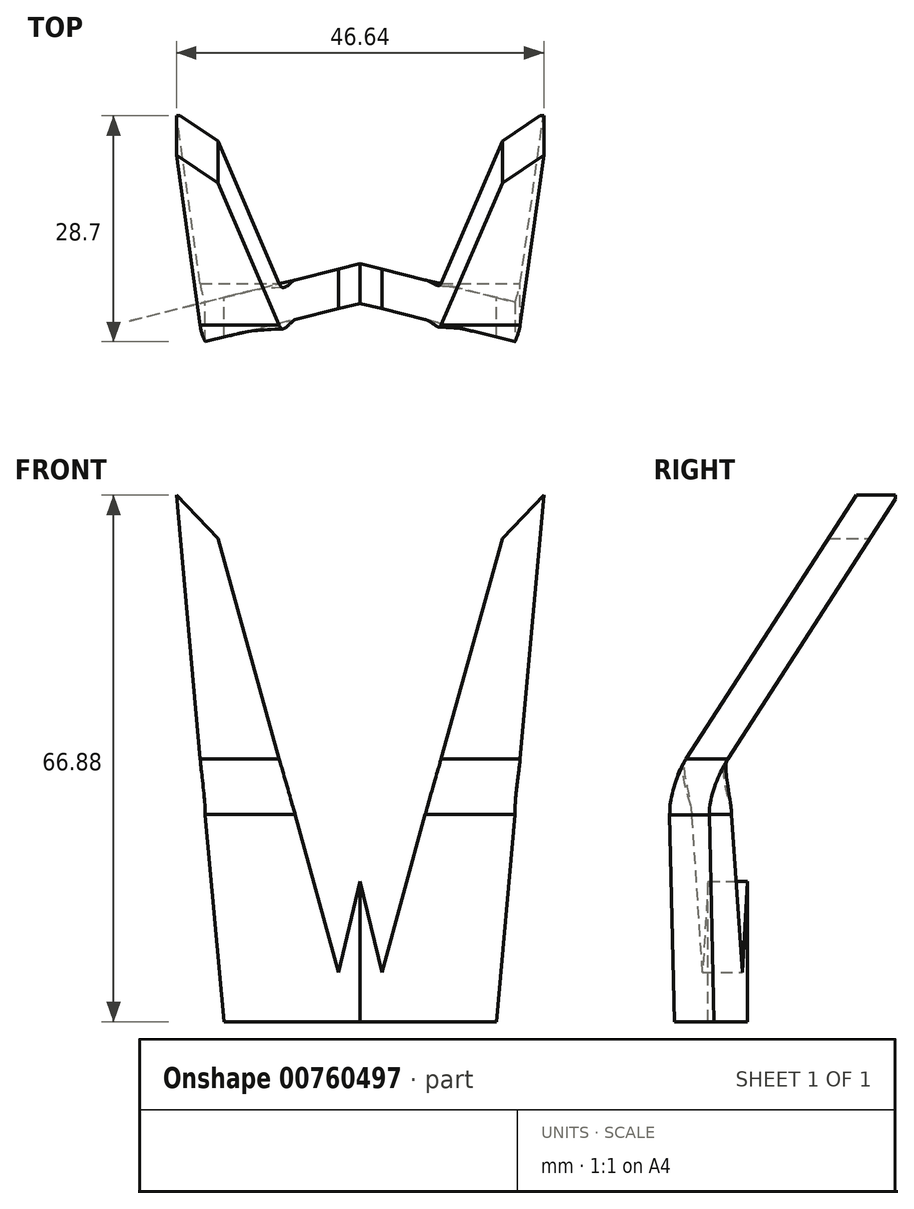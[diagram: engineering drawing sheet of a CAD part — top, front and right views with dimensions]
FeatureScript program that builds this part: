
annotation { "Feature Type Name" : "Feature", "Feature Type Description" : "" }
export const myFeature = defineFeature(function(context is Context, id is Id, definition is map)
    precondition{}
    {
        {
            var Q0;
            Q0=qCreatedBy(makeId("Front.planeOp"),FACE);
            var sketch = newSketch(context, id + "F0", { "sketchPlane" : qUnion([Q0])});
            skPoint(sketch, "E0.end.orphan", {"position": v(-20.31, 0) * mm});
            skLineSegment(sketch, "E1", {"start": v(-19.7, -7.18) * mm, "end": v(-18.06, -25.46) * mm});
            skLineSegment(sketch, "E2", {"start": v(-18.06, 27.96) * mm, "end": v(-23.32, 33.48) * mm});
            skLineSegment(sketch, "E3", {"start": v(-18.06, -25.46) * mm, "end": v(0, -33.48) * mm});
            skLineSegment(sketch, "E4.MirrorCS", {"start": v(18.06, 27.96) * mm, "end": v(23.32, 33.48) * mm});
            skLineSegment(sketch, "E5.MirrorCS", {"start": v(23.32, 33.48) * mm, "end": v(20.33, 0) * mm});
            skLineSegment(sketch, "E6.MirrorCS", {"start": v(18.06, -25.46) * mm, "end": v(0, -33.48) * mm});
            skPoint(sketch, "E7.MirrorCS.end.orphan", {"position": v(6.52, -25.46) * mm});
            skPoint(sketch, "E7.MirrorCS.start.orphan", {"position": v(18.06, 27.96) * mm});
            skLineSegment(sketch, "E8", {"start": v(-18.06, 27.96) * mm, "end": v(-10.27, 0) * mm});
            skPoint(sketch, "E8.endSnap0", {"position": v(-3.26, -18.56) * mm});
            skPoint(sketch, "E9.orphan", {"position": v(-6.52, -25.46) * mm});
            skPoint(sketch, "E10.orphan", {"position": v(0, -11.66) * mm});
            skLineSegment(sketch, "E11", {"start": v(0, -11.66) * mm, "end": v(-3.26, -25.2) * mm});
            skLineSegment(sketch, "E12.MirrorCS", {"start": v(18.06, 27.96) * mm, "end": v(10.27, 0) * mm});
            skLineSegment(sketch, "E13.MirrorCS", {"start": v(0, -11.66) * mm, "end": v(3.26, -25.2) * mm});
            skLineSegment(sketch, "E14", {"start": v(-20.31, 0) * mm, "end": v(-10.27, 0) * mm});
            skLineSegment(sketch, "E15.trimOffspring", {"start": v(10.27, 0) * mm, "end": v(20.33, 0) * mm});
            skLineSegment(sketch, "E16", {"start": v(-19.7, -7.18) * mm, "end": v(-8.28, -7.18) * mm});
            skLineSegment(sketch, "E17.trimOffspring", {"start": v(8.28, -7.18) * mm, "end": v(19.7, -7.18) * mm});
            skLineSegment(sketch, "E18.trimOffspring", {"start": v(8.28, -7.18) * mm, "end": v(3.26, -25.2) * mm});
            skLineSegment(sketch, "E19.trimOffspring", {"start": v(19.7, -7.18) * mm, "end": v(18.06, -25.46) * mm});
            skLineSegment(sketch, "E20.trimOffspring", {"start": v(-8.28, -7.18) * mm, "end": v(-3.26, -25.2) * mm});
            skLineSegment(sketch, "E21", {"start": v(-23.32, 33.48) * mm, "end": v(-20.31, 0) * mm});
            skLineSegment(sketch, "E22", {"start": v(0, -33.48) * mm, "end": v(0, -11.66) * mm});
            skPoint(sketch, "E23", {"position": v(-18.06, -25.46) * mm});
            skPoint(sketch, "E24", {"position": v(18.06, -25.46) * mm});
            skPoint(sketch, "E25", {"position": v(0, -33.48) * mm});
            skSolve(sketch);
        }
        {
            var Q0;
            Q0=makeQuery(id+"F0.imprint","IMPRINT",FACE,{"disambiguationData":[TD([[makeQuery(id+"F0.imprint","IMPRINT",EDGE,{"derivedFrom":sQuery(id+"F0.wireOp",EDGE,"E2")}),1.0]])]});
            var Q1;
            Q1=makeQuery(id+"F0.imprint","IMPRINT",FACE,{"disambiguationData":[TD([[makeQuery(id+"F0.imprint","IMPRINT",EDGE,{"derivedFrom":sQuery(id+"F0.wireOp",EDGE,"E4.MirrorCS")}),-1.0]])]});
            var Q2;
            Q2=makeQuery(id+"F0.imprint","IMPRINT",FACE,{"disambiguationData":[TD([[makeQuery(id+"F0.imprint","IMPRINT",EDGE,{"derivedFrom":sQuery(id+"F0.wireOp",EDGE,"E6.MirrorCS")}),-1.0]])]});
            extrude(context, id + "F1", {"entities" : qUnion([Q0, Q1, Q2]), "endBound" : BoundingType.SYMMETRIC, "depth" : 37.6 * mm, "offsetDistance" : 25 * mm});
        }
        {
            var Q0;
            Q0=qCreatedBy(makeId("Top.planeOp"),FACE);
            var sketch = newSketch(context, id + "F2", { "sketchPlane" : qUnion([Q0])});
            skPoint(sketch, "E26.start.orphan", {"position": v(0, -5.03) * mm});
            skLineSegment(sketch, "E27", {"start": v(0, 0) * mm, "end": v(-19.67, -4.87) * mm});
            skLineSegment(sketch, "E28", {"start": v(0, -5.03) * mm, "end": v(-19.67, -9.9) * mm});
            skLineSegment(sketch, "E29", {"start": v(-19.67, -4.87) * mm, "end": v(-19.67, -9.9) * mm});
            skPoint(sketch, "E30.orphan", {"position": v(-25.22, -11.28) * mm});
            skPoint(sketch, "E31.orphan", {"position": v(-25.22, -6.25) * mm});
            skPoint(sketch, "E32.orphan", {"position": v(-19.67, 0) * mm});
            skLineSegment(sketch, "E33.MirrorCS", {"start": v(0, -5.03) * mm, "end": v(19.67, -9.9) * mm});
            skLineSegment(sketch, "E34.MirrorCS", {"start": v(0, 0) * mm, "end": v(19.67, -4.87) * mm});
            skLineSegment(sketch, "E35.MirrorCS", {"start": v(19.67, -4.87) * mm, "end": v(19.67, -9.9) * mm});
            skSolve(sketch);
        }
        {
            var Q0;
            Q0 = qSketchRegion(id + "F2", true);
            extrude(context, id + "F3", {"entities" : qUnion([Q0]), "oppositeDirection" : true, "depth" : 33.4 * mm, "offsetDistance" : 25 * mm});
        }
        {
            var Q0;
            Q0=qCreatedBy(makeId("Front.planeOp"),FACE);
            var sketch = newSketch(context, id + "F4", { "sketchPlane" : qUnion([Q0])});
            skLineSegment(sketch, "E36", {"start": v(-23.28, 33.1) * mm, "end": v(-20.3, 0) * mm});
            skLineSegment(sketch, "E37", {"start": v(-21.35, -35.83) * mm, "end": v(-17.1, -35.83) * mm});
            skLineSegment(sketch, "E38", {"start": v(-20.3, 0) * mm, "end": v(-21.35, -35.83) * mm});
            skLineSegment(sketch, "E39", {"start": v(-19.68, -7.05) * mm, "end": v(0, -7.05) * mm});
            skLineSegment(sketch, "E40", {"start": v(0, -7.05) * mm, "end": v(0, 0) * mm});
            skLineSegment(sketch, "E41", {"start": v(0, 0) * mm, "end": v(-20.3, 0) * mm});
            skLineSegment(sketch, "E42.trimOffspring", {"start": v(-19.68, -7.05) * mm, "end": v(-17.1, -35.83) * mm});
            skLineSegment(sketch, "E43.MirrorCS", {"start": v(20.3, 0) * mm, "end": v(21.35, -35.83) * mm});
            skLineSegment(sketch, "E44.MirrorCS", {"start": v(19.68, -7.05) * mm, "end": v(17.1, -35.83) * mm});
            skLineSegment(sketch, "E45.MirrorCS", {"start": v(21.35, -35.83) * mm, "end": v(17.1, -35.83) * mm});
            skLineSegment(sketch, "E46.MirrorCS", {"start": v(19.68, -7.05) * mm, "end": v(0, -7.05) * mm});
            skLineSegment(sketch, "E47.MirrorCS", {"start": v(0, 0) * mm, "end": v(20.3, 0) * mm});
            skSolve(sketch);
        }
        {
            var Q0;
            Q0=makeQuery(id+"F1.opExtrude","SWEPT_BODY",BODY,{"disambiguationData":[OSD([sQuery(id+"F0.wireOp",EDGE,"E6.MirrorCS"),sQuery(id+"F0.wireOp",EDGE,"E13.MirrorCS"),sQuery(id+"F0.wireOp",EDGE,"E17.trimOffspring"),sQuery(id+"F0.wireOp",EDGE,"E18.trimOffspring"),sQuery(id+"F0.wireOp",EDGE,"E19.trimOffspring"),sQuery(id+"F0.wireOp",EDGE,"E22")])]});
            deleteBodies(context, id + "F5", {"entities" : qUnion([Q0])});
        }
        {
            var Q0;
            Q0=qCreatedBy(makeId("Front.planeOp"),FACE);
            var sketch = newSketch(context, id + "F6", { "sketchPlane" : qUnion([Q0])});
            skLineSegment(sketch, "E48", {"start": v(-10.63, 1.57) * mm, "end": v(-10.2, 0) * mm});
            skLineSegment(sketch, "E49", {"start": v(-2.77, -27.16) * mm, "end": v(0, -15.55) * mm});
            skLineSegment(sketch, "E50.MirrorCS", {"start": v(2.77, -27.16) * mm, "end": v(0, -15.55) * mm});
            skLineSegment(sketch, "E51.MirrorCS", {"start": v(17.82, 27.87) * mm, "end": v(10.2, 0) * mm});
            skLineSegment(sketch, "E52", {"start": v(-10.63, 1.57) * mm, "end": v(10.63, 1.57) * mm});
            skPoint(sketch, "E53.orphan", {"position": v(-17.82, 27.87) * mm});
            skLineSegment(sketch, "E54", {"start": v(-20.97, -7.1) * mm, "end": v(-8.26, -7.1) * mm});
            skLineSegment(sketch, "E55", {"start": v(22.74, -7.1) * mm, "end": v(22.74, 0) * mm});
            skLineSegment(sketch, "E56", {"start": v(22.74, 0) * mm, "end": v(-22.12, 0) * mm});
            skLineSegment(sketch, "E57", {"start": v(-22.12, 0) * mm, "end": v(-20.97, -7.1) * mm});
            skLineSegment(sketch, "E58.trimOffspring", {"start": v(-8.26, -7.1) * mm, "end": v(-2.77, -27.16) * mm});
            skLineSegment(sketch, "E59.trimOffspring", {"start": v(8.26, -7.1) * mm, "end": v(2.77, -27.16) * mm});
            skLineSegment(sketch, "E60.trimOffspring", {"start": v(8.26, -7.1) * mm, "end": v(22.74, -7.1) * mm});
            skSolve(sketch);
        }
        {
            var Q0;
            Q0 = qSketchRegion(id + "F6", true);
            extrude(context, id + "F7", {"entities" : qUnion([Q0]), "operationType" : NewBodyOperationType.REMOVE, "depth" : 13.3 * mm, "offsetDistance" : 25 * mm});
        }
        {
            var Q0;
            Q0 = qSketchRegion(id + "F4", true);
            extrude(context, id + "F8", {"entities" : qUnion([Q0]), "operationType" : NewBodyOperationType.REMOVE, "oppositeDirection" : true, "depth" : 25 * mm, "offsetDistance" : 25 * mm});
        }
        {
            var Q0;
            Q0 = qSketchRegion(id + "F4", true);
            extrude(context, id + "F9", {"entities" : qUnion([Q0]), "operationType" : NewBodyOperationType.REMOVE, "depth" : 25 * mm, "offsetDistance" : 25 * mm});
        }
        {
            var Q0;
            Q0=qCreatedBy(makeId("Right.planeOp"),FACE);
            var sketch = newSketch(context, id + "F10", { "sketchPlane" : qUnion([Q0])});
            skPoint(sketch, "E61.orphan", {"position": v(0, -7.4) * mm});
            skLineSegment(sketch, "E62", {"start": v(-7.8, 0) * mm, "end": v(15.55, 36.16) * mm});
            skLineSegment(sketch, "E63", {"start": v(-2.5, 0) * mm, "end": v(20.86, 36.16) * mm});
            skPoint(sketch, "E64.start.orphan", {"position": v(-9.96, -7.4) * mm});
            skPoint(sketch, "E65.end.orphan", {"position": v(-4.98, -7.4) * mm});
            skLineSegment(sketch, "E66", {"start": v(-20.85, 0) * mm, "end": v(-20.85, 36.16) * mm});
            skLineSegment(sketch, "E67", {"start": v(-20.85, 36.16) * mm, "end": v(15.55, 36.16) * mm});
            skLineSegment(sketch, "E68", {"start": v(20.86, 36.16) * mm, "end": v(20.86, 0) * mm});
            skLineSegment(sketch, "E69", {"start": v(-20.85, 0) * mm, "end": v(-20.85, -9.55) * mm});
            skLineSegment(sketch, "E70", {"start": v(-20.85, -9.55) * mm, "end": v(-7.8, 0) * mm});
            skLineSegment(sketch, "E71", {"start": v(-2.5, 0) * mm, "end": v(21.43, -5.11) * mm});
            skLineSegment(sketch, "E72", {"start": v(21.43, -5.11) * mm, "end": v(20.86, 0) * mm});
            skSolve(sketch);
        }
        {
            var Q0;
            Q0 = qSketchRegion(id + "F10", true);
            extrude(context, id + "F11", {"entities" : qUnion([Q0]), "operationType" : NewBodyOperationType.REMOVE, "endBound" : BoundingType.SYMMETRIC, "oppositeDirection" : true, "depth" : 74 * mm, "offsetDistance" : 25 * mm});
        }
        {
            var Q0;
            Q0=makeQuery(id+"F7.boolean.opBoolean","COPY",FACE,{"derivedFrom":makeQuery(id+"F7.opExtrude","SWEPT_FACE",FACE,{"disambiguationData":[OSD([sQuery(id+"F6.wireOp",EDGE,"E54")])]})});
            var Q1;
            Q1=makeQuery(id+"F1.opExtrude","SWEPT_FACE",FACE,{"disambiguationData":[OSD([sQuery(id+"F0.wireOp",EDGE,"E14")])]});
            var Q2;
            Q2=makeQuery(id+"F11.boolean.opBoolean","INTERSECT",VERTEX,{"derivedFrom":[makeQuery(id+"F1.opExtrude","SWEPT_FACE",FACE,{"disambiguationData":[OSD([sQuery(id+"F0.wireOp",EDGE,"E21")])]}),makeQuery(id+"F11.opExtrude","SWEPT_FACE",FACE,{"disambiguationData":[OSD([sQuery(id+"F10.wireOp",EDGE,"E62")])]})]});
            var Q3;
            Q3=makeQuery(id+"F7.boolean.opBoolean","INTERSECT",VERTEX,{"derivedFrom":[makeQuery(id+"F3.opExtrude","SWEPT_FACE",FACE,{"disambiguationData":[OSD([sQuery(id+"F2.wireOp",EDGE,"E28")])]}),makeQuery(id+"F3.opExtrude","SWEPT_FACE",FACE,{"disambiguationData":[OSD([sQuery(id+"F2.wireOp",EDGE,"E29")])]}),makeQuery(id+"F7.opExtrude","SWEPT_FACE",FACE,{"disambiguationData":[OSD([sQuery(id+"F6.wireOp",EDGE,"E54")])]})]});
            loft(context, id + "F12", {"operationType" : NewBodyOperationType.ADD, "startCondition" : LoftEndDerivativeType.MATCH_CURVATURE, "startMagnitude" : 0.5, "endCondition" : LoftEndDerivativeType.MATCH_CURVATURE, "endMagnitude" : 0.9, "sheetProfilesArray" : [{ "sheetProfileEntities" : qUnion([Q0]) }, { "sheetProfileEntities" : qUnion([Q1]) }], "connections" : [{ "connectionEntities" : qUnion([Q2, Q3]), "connectionEdgeQueries" : qUnion([]), "connectionEdgeParameters" : [] }]});
        }
        {
            var Q0;
            Q0=makeQuery(id+"F1.opExtrude","SWEPT_FACE",FACE,{"disambiguationData":[OSD([sQuery(id+"F0.wireOp",EDGE,"E15.trimOffspring")])]});
            var Q1;
            Q1=makeQuery(id+"F7.boolean.opBoolean","COPY",FACE,{"derivedFrom":makeQuery(id+"F7.opExtrude","SWEPT_FACE",FACE,{"disambiguationData":[OSD([sQuery(id+"F6.wireOp",EDGE,"E60.trimOffspring")])]})});
            loft(context, id + "F13", {"operationType" : NewBodyOperationType.ADD, "startCondition" : LoftEndDerivativeType.MATCH_CURVATURE, "startMagnitude" : .5, "endCondition" : LoftEndDerivativeType.MATCH_CURVATURE, "endMagnitude" : .9, "sheetProfilesArray" : [{ "sheetProfileEntities" : qUnion([Q0]) }, { "sheetProfileEntities" : qUnion([Q1]) }]});
        }
    });
